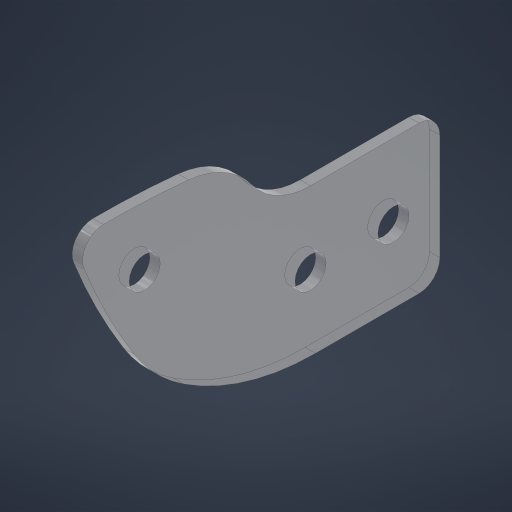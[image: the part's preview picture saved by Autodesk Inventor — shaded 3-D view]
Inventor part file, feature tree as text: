
AUTODESK INVENTOR PART (.ipt)
format: ipt  version: 2024 (Build 280153000, 153)  size: 223,232 bytes
history: native  units: in
note: dims shown in document units (in); Inventor stores cm internally (conversion verified against a paired STEP export)
features: sketch x1, extrude x1, hole x1
ambient origin geometry x8: Origin, YZ Plane, XZ Plane, XY Plane, X Axis, Y Axis, Z Axis, Center Point
bodies: Solid1 (feature_tree)
feature tree (3):
  sketch  "Sketch2"  dims[d0=1.0in d1=0.5in d2=0.25in d3=0.25in d4=1.25in d5=1.0in d7=1.0in d8=0.5in d12=1.0in d17=0.75in d18=1.0in d19=0.0625in d20=0.0in d21=0.125in d22=0.1875in d23=0.75in d24=0.375in d25=0.25in d26=0.5635in d27=1.0in d28=0.8108in d29=0.5in]
  extrude  "Extrusion1"  Depth=1.0in
  hole  "Hole1"  [1 undecoded]
note: 1 required parameter value undecoded (feature->parameter linkage not recoverable at this tier; creation-order binding heuristic only, values carry confidence <= 0.55)
